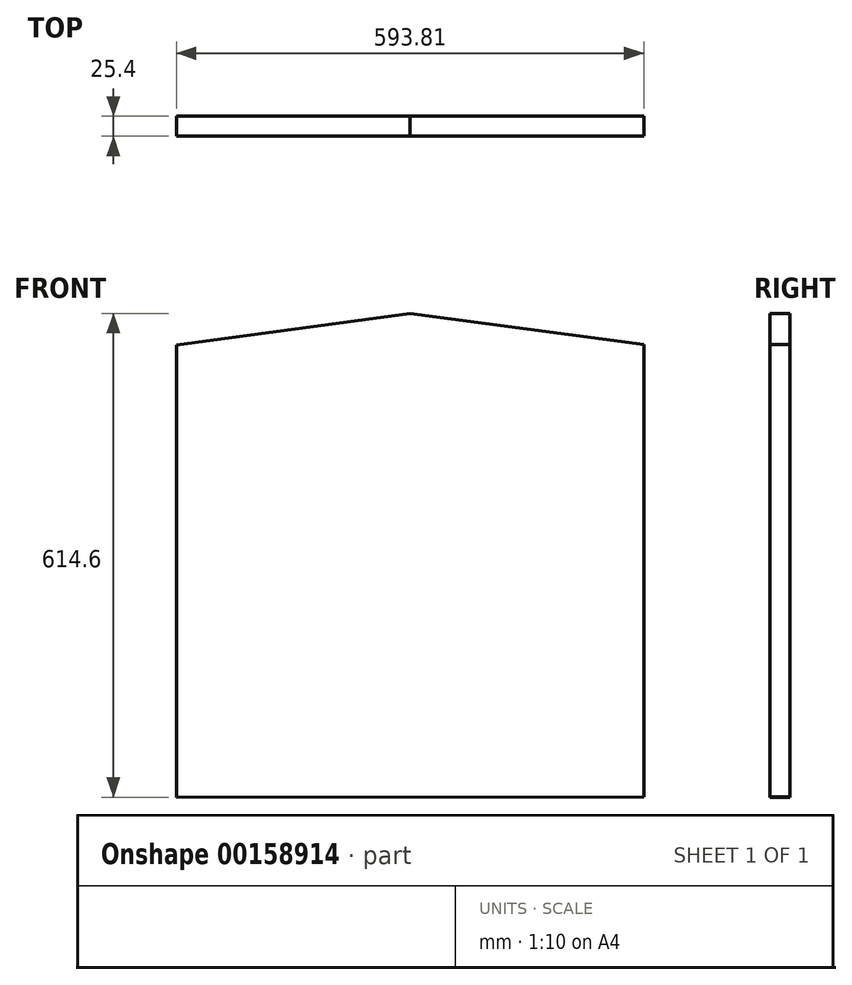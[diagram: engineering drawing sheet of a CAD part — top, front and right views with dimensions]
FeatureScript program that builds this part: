
annotation { "Feature Type Name" : "Feature", "Feature Type Description" : "" }
export const myFeature = defineFeature(function(context is Context, id is Id, definition is map)
    precondition{}
    {
        {
            var Q0;
            Q0=qCreatedBy(makeId("Front.planeOp"),FACE);
            var sketch = newSketch(context, id + "F0", { "sketchPlane" : qUnion([Q0])});
            skPoint(sketch, "E0.orphan", {"position": v(-0.8, 572.32) * mm});
            skPoint(sketch, "E1.orphan", {"position": v(565.94, 572.32) * mm});
            skLineSegment(sketch, "E2.0", {"start": v(283.33, 585.17) * mm, "end": v(-13.53, 545.25) * mm});
            skLineSegment(sketch, "E3.0", {"start": v(283.33, 585.17) * mm, "end": v(580.28, 545.85) * mm});
            skLineSegment(sketch, "E4.0", {"start": v(580.2, -28.83) * mm, "end": v(580.28, 545.85) * mm});
            skLineSegment(sketch, "E5.0", {"start": v(-13.53, -29.43) * mm, "end": v(-13.53, 545.25) * mm});
            skLineSegment(sketch, "E6.0", {"start": v(-13.53, -29.43) * mm, "end": v(580.2, -28.83) * mm});
            skSolve(sketch);
        }
        {
            var Q0;
            Q0 = qSketchRegion(id + "F0", true);
            extrude(context, id + "F1", {"entities" : qUnion([Q0]), "depth" : 25.4 * mm});
        }
    });
